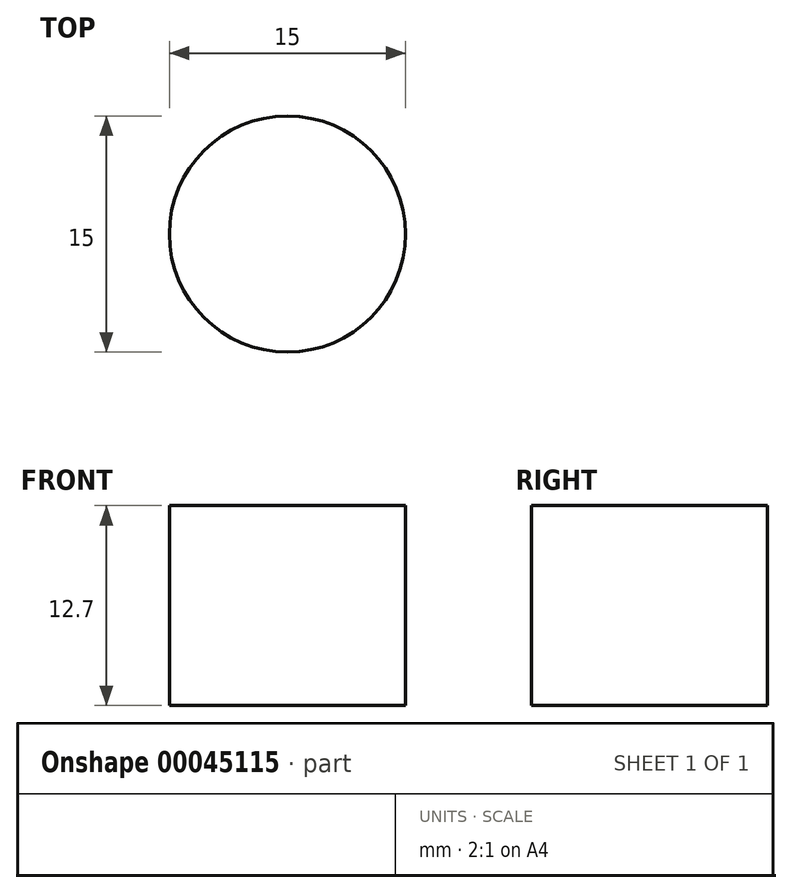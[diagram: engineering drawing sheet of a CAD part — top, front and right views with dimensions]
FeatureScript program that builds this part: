
annotation { "Feature Type Name" : "Feature", "Feature Type Description" : "" }
export const myFeature = defineFeature(function(context is Context, id is Id, definition is map)
    precondition{}
    {
        {
            var Q0;
            Q0=qCreatedBy(makeId("Top.planeOp"),FACE);
            var sketch = newSketch(context, id + "F0", { "sketchPlane" : qUnion([Q0])});
            skCircle(sketch, "E0", {"center": v(0, 0) * mm, "radius": 7.5 * mm});
            skSolve(sketch);
        }
        {
            var Q0;
            Q0=makeQuery(id+"F0.imprint","IMPRINT",FACE,{"disambiguationData":[TD([[makeQuery(id+"F0.imprint","IMPRINT",EDGE,{"derivedFrom":sQuery(id+"F0.wireOp",EDGE,"E0")}),1.0]])]});
            extrude(context, id + "F1", {"entities" : qUnion([Q0]), "depth" : 12.7 * mm});
        }
    });
